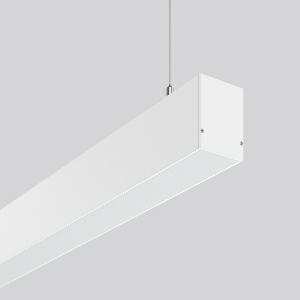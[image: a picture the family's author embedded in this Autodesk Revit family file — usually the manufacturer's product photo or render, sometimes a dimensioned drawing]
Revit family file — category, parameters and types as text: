
# Revit family: less_is_more_50_312311_002_1_76_7718
name_source: partatom
category: Lighting Fixtures
units: mm (PartAtom-declared; Revit-internal decimal feet)

## family parameters
Cut with Voids When Loaded = No
Host = Face
Light Source = No
Part Type = Normal
Room Calculation Point = No
Round Connector Dimension = Use Diameter
Shared = No

## types (1)
- LESS IS MORE 50 (1 x LED Modul 840, 2400 lm, 4000)
    Apparent Load = 22 VA
    CIE Flux Codes = 48 79 95 100 100
    Color Rendering = 80
    Color Temperature = 4000
    Default Elevation = 1800 mm
    Description = Series: LESS IS MORE 50
Linear pendant luminaire for aesthetically sophisticated lighting. Housing: extruded aluminium profile, powder-coated. End cap aluminium powder-coated. Canopy made of aluminium, powder-coated. Diffuser made of non-yellowing plastic (PMMA), opal. Direct light emission. Suitable for pendant. 2-point steel cable suspension freely positionable and infinitely height-adjustable. Special lengths available on request. LED unit with integrated converter interchangeable and removable. Suitable for through-wiring. With sensors or as a safety luminaire on request. 
Colour: traffic white, matt (RAL 9016)
Length: 847 mm
Width: 57 mm
Height: 75 mm
Suspension length: 2000 mm
Lamp: LED
Socket: without socket
Colour temperature: 4000K
Colour rendering index (CRI): 80
System power: 22 W
Rated luminous flux: 2400 lm
Luminous efficiency: 109 lm/W
Control gear: Converter, dimmable, DALI
Protection class: I
Type of protection: IP 20
    Height = 75 mm
    Lamp = 1 x LED Modul 840
    Lamp Light Flux = 2400 lm
    Lamp count = 1
    Length = 847 mm
    Lifetime = 50000 h
    Luminous efficacy = 109 lm/W
    Manufacturer = RZB
    ModVariant = No
    Model = 312311.002.1.76
    Mounting Place = Ceiling
    Mounting Type = Pendant
    Number of Poles = 1
    OnlyDefault = Yes
    Power Factor = 1
    Product Name = LESS IS MORE 50
    Product group = Pendant LED linear luminaires
    ProductGroupID = 907
    Protection Class = Protection class I
    Protection Degree = IP 20
    RLX_Detail_Level = 1
    RLX_Emergency_Light_Flux = 0 lm
    RLX_Emergency_Type = 0
    RLX_Emergency_Type_DB = No
    RlxData = <blob elided: 20577 chars, md5=1161b2c5>
    Socket = socket
    Standby Power = 0 W
    System Light Flux = 2400 lm
    System Power = 22 W
    Type Comments = Product without accessories
    Type Image = 312318.002.jpg
    URL = http://relux.com
    VarID = ---
    Voltage = 230 V
    Voltage Range = 220-240 V
    Weight = 0.00 kg
    Width = 57 mm

## geometry (parser evidence)
native form markers: Blend x4, Sweep x10
no freeform markers — native parametric forms only
